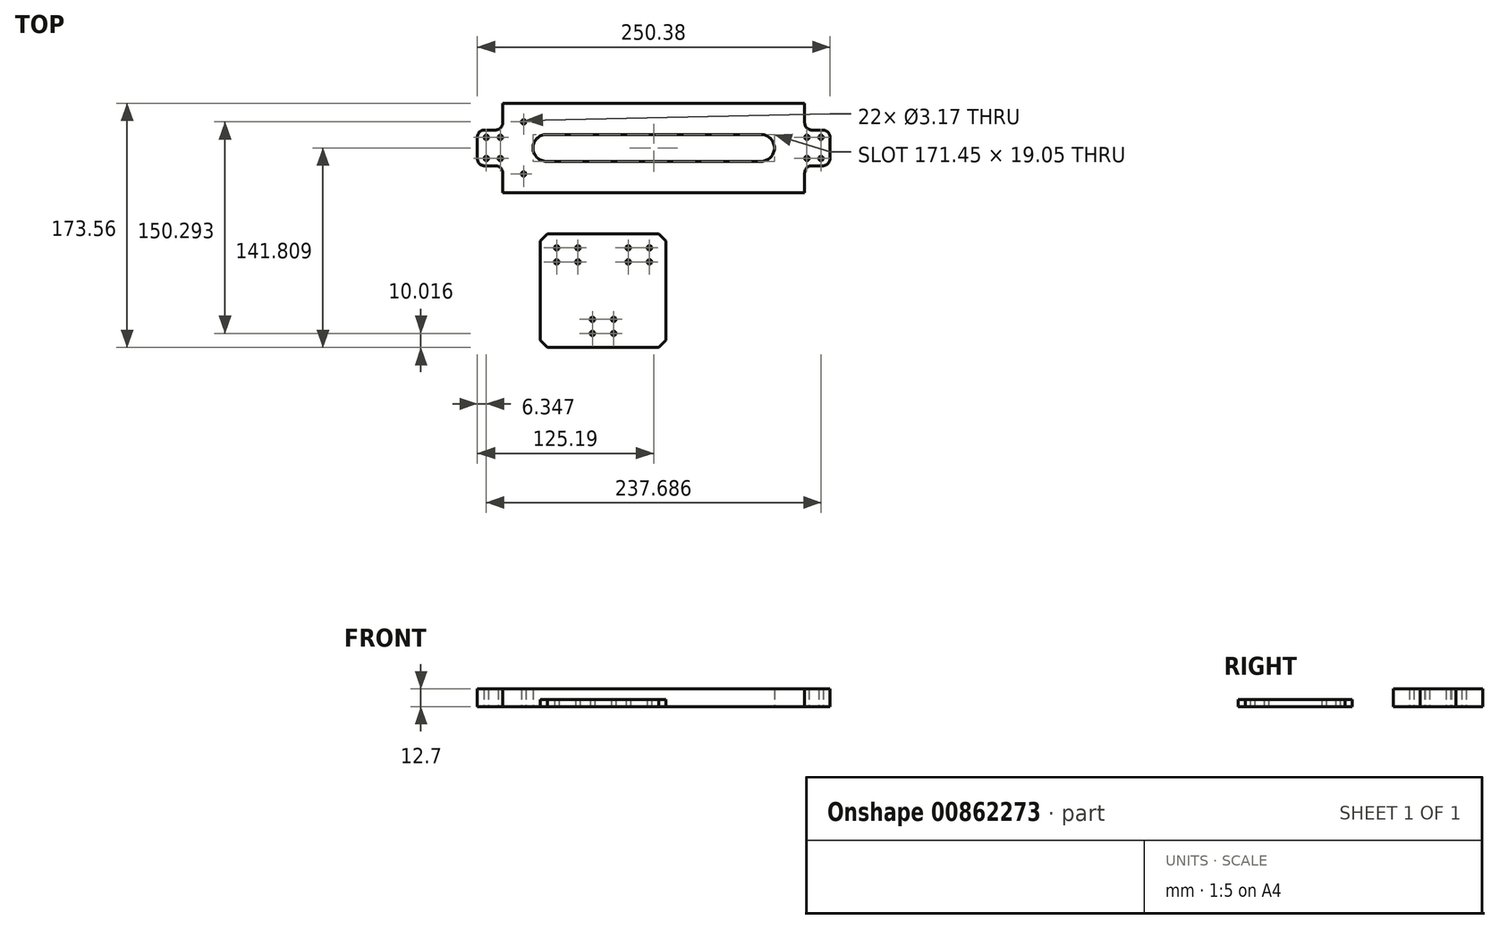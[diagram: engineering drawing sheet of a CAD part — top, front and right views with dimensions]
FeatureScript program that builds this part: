
annotation { "Feature Type Name" : "Feature", "Feature Type Description" : "" }
export const myFeature = defineFeature(function(context is Context, id is Id, definition is map)
    precondition{}
    {
        {
            var Q0;
            Q0=qCreatedBy(makeId("Top.planeOp"),FACE);
            var sketch = newSketch(context, id + "F0", { "sketchPlane" : qUnion([Q0])});
            skLineSegment(sketch, "E0.bottom", {"start": v(-50.02, 48.8) * mm, "end": v(-40.02, 48.8) * mm, "construction": true});
            skLineSegment(sketch, "E0.top", {"start": v(-50.02, 33.8) * mm, "end": v(-40.02, 33.8) * mm, "construction": true});
            skLineSegment(sketch, "E0.left", {"start": v(-50.02, 48.8) * mm, "end": v(-50.02, 33.8) * mm, "construction": true});
            skLineSegment(sketch, "E0.right", {"start": v(-40.02, 48.8) * mm, "end": v(-40.02, 33.8) * mm, "construction": true});
            skPoint(sketch, "E0.middle", {"position": v(-45.02, 41.3) * mm});
            skLineSegment(sketch, "E1.bottom", {"start": v(177.66, 48.8) * mm, "end": v(187.66, 48.8) * mm, "construction": true});
            skLineSegment(sketch, "E1.top", {"start": v(177.66, 33.8) * mm, "end": v(187.66, 33.8) * mm, "construction": true});
            skLineSegment(sketch, "E1.left", {"start": v(177.66, 48.8) * mm, "end": v(177.66, 33.8) * mm, "construction": true});
            skLineSegment(sketch, "E1.right", {"start": v(187.66, 48.8) * mm, "end": v(187.66, 33.8) * mm, "construction": true});
            skPoint(sketch, "E1.middle", {"position": v(182.66, 41.3) * mm});
            skCircle(sketch, "E2", {"center": v(-50.02, 48.8) * mm, "radius": 1.59 * mm});
            skCircle(sketch, "E3", {"center": v(-40.02, 48.8) * mm, "radius": 1.59 * mm});
            skCircle(sketch, "E4", {"center": v(-40.02, 33.8) * mm, "radius": 1.59 * mm});
            skCircle(sketch, "E5", {"center": v(-50.02, 33.8) * mm, "radius": 1.59 * mm});
            skCircle(sketch, "E6", {"center": v(177.66, 33.8) * mm, "radius": 1.59 * mm});
            skCircle(sketch, "E7", {"center": v(187.66, 33.8) * mm, "radius": 1.59 * mm});
            skCircle(sketch, "E8", {"center": v(187.66, 48.8) * mm, "radius": 1.59 * mm});
            skCircle(sketch, "E9", {"center": v(177.66, 48.8) * mm, "radius": 1.59 * mm});
            skLineSegment(sketch, "E10", {"start": v(-45.02, 41.3) * mm, "end": v(182.66, 41.3) * mm, "construction": true});
            skLineSegment(sketch, "E11.bottom", {"start": v(16.5, 66.7) * mm, "end": v(121.14, 66.7) * mm, "construction": true});
            skLineSegment(sketch, "E11.top", {"start": v(16.5, 15.9) * mm, "end": v(121.14, 15.9) * mm, "construction": true});
            skLineSegment(sketch, "E11.left", {"start": v(16.5, 66.7) * mm, "end": v(16.5, 15.9) * mm, "construction": true});
            skLineSegment(sketch, "E11.right", {"start": v(121.14, 66.7) * mm, "end": v(121.14, 15.9) * mm, "construction": true});
            skPoint(sketch, "E11.middle", {"position": v(68.82, 41.3) * mm});
            skLineSegment(sketch, "E12", {"start": v(-56.37, 54) * mm, "end": v(-56.37, 28.6) * mm});
            skLineSegment(sketch, "E13", {"start": v(-56.37, 28.6) * mm, "end": v(-38.44, 28.6) * mm});
            skLineSegment(sketch, "E14", {"start": v(-38.44, 28.6) * mm, "end": v(-38.44, 9.55) * mm});
            skLineSegment(sketch, "E15", {"start": v(-38.44, 9.55) * mm, "end": v(176.08, 9.55) * mm});
            skLineSegment(sketch, "E16", {"start": v(176.08, 9.55) * mm, "end": v(176.08, 28.6) * mm});
            skLineSegment(sketch, "E17", {"start": v(176.08, 28.6) * mm, "end": v(194.01, 28.6) * mm});
            skLineSegment(sketch, "E18", {"start": v(194.01, 28.6) * mm, "end": v(194.01, 54) * mm});
            skLineSegment(sketch, "E19", {"start": v(194.01, 54) * mm, "end": v(176.08, 54) * mm});
            skLineSegment(sketch, "E20", {"start": v(176.08, 54) * mm, "end": v(176.08, 73.05) * mm});
            skLineSegment(sketch, "E21", {"start": v(176.08, 73.05) * mm, "end": v(-38.44, 73.05) * mm});
            skLineSegment(sketch, "E22", {"start": v(-38.44, 73.05) * mm, "end": v(-38.44, 54) * mm});
            skPoint(sketch, "E22.endSnap0", {"position": v(185.04, 54) * mm});
            skLineSegment(sketch, "E23", {"start": v(-38.44, 54) * mm, "end": v(-56.37, 54) * mm});
            skPoint(sketch, "E24", {"position": v(68.82, 73.05) * mm});
            skPoint(sketch, "E25", {"position": v(-56.37, 41.3) * mm});
            skLineSegment(sketch, "E26", {"start": v(-7.38, 41.3) * mm, "end": v(145.02, 41.3) * mm});
            skArc(sketch, "E27.0.startCap", {"start": v(-7.38, 31.77) * mm, "mid": v(-16.9, 41.3) * mm, "end": v(-7.38, 50.82) * mm});
            skArc(sketch, "E27.0.endCap", {"start": v(145.02, 50.82) * mm, "mid": v(154.54, 41.3) * mm, "end": v(145.02, 31.77) * mm});
            skLineSegment(sketch, "E27.0.left", {"start": v(-7.38, 50.82) * mm, "end": v(145.02, 50.82) * mm});
            skLineSegment(sketch, "E27.0.right", {"start": v(-7.38, 31.77) * mm, "end": v(145.02, 31.77) * mm});
            skLineSegment(sketch, "E28", {"start": v(-23.54, 59.8) * mm, "end": v(-23.54, 22.8) * mm, "construction": true});
            skPoint(sketch, "E29", {"position": v(-23.54, 41.3) * mm});
            skCircle(sketch, "E30", {"center": v(-23.54, 59.8) * mm, "radius": 1.59 * mm});
            skCircle(sketch, "E31", {"center": v(-23.54, 22.8) * mm, "radius": 1.59 * mm});
            skSolve(sketch);
        }
        {
            var Q0;
            Q0=makeQuery(id+"F0.imprint","IMPRINT",FACE,{"disambiguationData":[TD([[makeQuery(id+"F0.imprint","IMPRINT",EDGE,{"derivedFrom":sQuery(id+"F0.wireOp",EDGE,"E2")}),-1.0]])]});
            extrude(context, id + "F1", {"entities" : qUnion([Q0]), "depth" : 12.7 * mm, "offsetDistance" : 25.4 * mm});
        }
        {
            var Q0;
            Q0=makeQuery(id+"F1.opExtrude","SWEPT_EDGE",EDGE,{"disambiguationData":[OSD([sQuery(id+"F0.wireOp",EDGE,"E22"),sQuery(id+"F0.wireOp",EDGE,"E23")])]});
            var Q1;
            Q1=makeQuery(id+"F1.opExtrude","SWEPT_EDGE",EDGE,{"disambiguationData":[OSD([sQuery(id+"F0.wireOp",EDGE,"E13"),sQuery(id+"F0.wireOp",EDGE,"E14")])]});
            var Q2;
            Q2=makeQuery(id+"F1.opExtrude","SWEPT_EDGE",EDGE,{"disambiguationData":[OSD([sQuery(id+"F0.wireOp",EDGE,"E16"),sQuery(id+"F0.wireOp",EDGE,"E17")])]});
            var Q3;
            Q3=makeQuery(id+"F1.opExtrude","SWEPT_EDGE",EDGE,{"disambiguationData":[OSD([sQuery(id+"F0.wireOp",EDGE,"E17"),sQuery(id+"F0.wireOp",EDGE,"E18")])]});
            var Q4;
            Q4=makeQuery(id+"F1.opExtrude","SWEPT_EDGE",EDGE,{"disambiguationData":[OSD([sQuery(id+"F0.wireOp",EDGE,"E18"),sQuery(id+"F0.wireOp",EDGE,"E19")])]});
            var Q5;
            Q5=makeQuery(id+"F1.opExtrude","SWEPT_EDGE",EDGE,{"disambiguationData":[OSD([sQuery(id+"F0.wireOp",EDGE,"E19"),sQuery(id+"F0.wireOp",EDGE,"E20")])]});
            var Q6;
            Q6=makeQuery(id+"F1.opExtrude","SWEPT_EDGE",EDGE,{"disambiguationData":[OSD([sQuery(id+"F0.wireOp",EDGE,"E12"),sQuery(id+"F0.wireOp",EDGE,"E13")])]});
            var Q7;
            Q7=makeQuery(id+"F1.opExtrude","SWEPT_EDGE",EDGE,{"disambiguationData":[OSD([sQuery(id+"F0.wireOp",EDGE,"E12"),sQuery(id+"F0.wireOp",EDGE,"E23")])]});
            fillet(context, id + "F2", {"entities" : qUnion([Q0, Q1, Q2, Q3, Q4, Q5, Q6, Q7]), "radius" : 5.08 * mm, "tangentPropagation" : true, "allowEdgeOverflow" : false});
        }
        {
            var Q0;
            Q0=qCreatedBy(makeId("Top.planeOp"),FACE);
            var sketch = newSketch(context, id + "F3", { "sketchPlane" : qUnion([Q0])});
            skLineSegment(sketch, "E32.bottom", {"start": v(-11.55, -19.68) * mm, "end": v(77.35, -19.68) * mm});
            skLineSegment(sketch, "E32.top", {"start": v(-11.55, -100.5) * mm, "end": v(77.35, -100.5) * mm});
            skLineSegment(sketch, "E32.left", {"start": v(-11.55, -19.68) * mm, "end": v(-11.55, -100.5) * mm});
            skLineSegment(sketch, "E32.right", {"start": v(77.35, -19.68) * mm, "end": v(77.35, -100.5) * mm});
            skPoint(sketch, "E32.middle", {"position": v(32.9, -60.1) * mm});
            skLineSegment(sketch, "E33.bottom", {"start": v(25.4, -80.5) * mm, "end": v(40.4, -80.5) * mm, "construction": true});
            skLineSegment(sketch, "E33.top", {"start": v(25.4, -90.5) * mm, "end": v(40.4, -90.5) * mm, "construction": true});
            skLineSegment(sketch, "E33.left", {"start": v(25.4, -80.5) * mm, "end": v(25.4, -90.5) * mm, "construction": true});
            skLineSegment(sketch, "E33.right", {"start": v(40.4, -80.5) * mm, "end": v(40.4, -90.5) * mm, "construction": true});
            skPoint(sketch, "E33.middle", {"position": v(32.9, -85.5) * mm});
            skLineSegment(sketch, "E34", {"start": v(32.9, -60.1) * mm, "end": v(32.9, -19.68) * mm, "construction": true});
            skLineSegment(sketch, "E35.bottom", {"start": v(0, -29.7) * mm, "end": v(15, -29.7) * mm, "construction": true});
            skLineSegment(sketch, "E35.top", {"start": v(0, -39.7) * mm, "end": v(15, -39.7) * mm, "construction": true});
            skLineSegment(sketch, "E35.left", {"start": v(0, -29.7) * mm, "end": v(0, -39.7) * mm, "construction": true});
            skLineSegment(sketch, "E35.right", {"start": v(15, -29.7) * mm, "end": v(15, -39.7) * mm, "construction": true});
            skPoint(sketch, "E35.middle", {"position": v(7.5, -34.7) * mm});
            skCircle(sketch, "E36", {"center": v(0, -29.7) * mm, "radius": 1.59 * mm});
            skCircle(sketch, "E37", {"center": v(0, -39.7) * mm, "radius": 1.59 * mm});
            skCircle(sketch, "E38", {"center": v(15, -39.7) * mm, "radius": 1.59 * mm});
            skCircle(sketch, "E39", {"center": v(15, -29.7) * mm, "radius": 1.59 * mm});
            skLineSegment(sketch, "E40", {"start": v(32.9, -85.5) * mm, "end": v(32.9, -100.5) * mm, "construction": true});
            skLineSegment(sketch, "E41", {"start": v(7.5, -34.7) * mm, "end": v(7.5, -19.68) * mm, "construction": true});
            skCircle(sketch, "E42", {"center": v(25.4, -80.5) * mm, "radius": 1.59 * mm});
            skCircle(sketch, "E43", {"center": v(40.4, -80.5) * mm, "radius": 1.59 * mm});
            skCircle(sketch, "E44", {"center": v(40.4, -90.5) * mm, "radius": 1.59 * mm});
            skCircle(sketch, "E45", {"center": v(25.4, -90.5) * mm, "radius": 1.59 * mm});
            skLineSegment(sketch, "E46.MirrorCS", {"start": v(50.8, -29.7) * mm, "end": v(50.8, -39.7) * mm, "construction": true});
            skLineSegment(sketch, "E47.MirrorCS", {"start": v(65.8, -29.7) * mm, "end": v(50.8, -29.7) * mm, "construction": true});
            skLineSegment(sketch, "E48.MirrorCS", {"start": v(65.8, -39.7) * mm, "end": v(50.8, -39.7) * mm, "construction": true});
            skLineSegment(sketch, "E49.MirrorCS", {"start": v(65.8, -29.7) * mm, "end": v(65.8, -39.7) * mm, "construction": true});
            skCircle(sketch, "E50.MirrorC", {"center": v(50.8, -39.7) * mm, "radius": 1.59 * mm});
            skCircle(sketch, "E51.MirrorC", {"center": v(65.8, -29.7) * mm, "radius": 1.59 * mm});
            skPoint(sketch, "E52.MirrorP", {"position": v(58.3, -34.7) * mm});
            skCircle(sketch, "E53.MirrorC", {"center": v(50.8, -29.7) * mm, "radius": 1.59 * mm});
            skCircle(sketch, "E54.MirrorC", {"center": v(65.8, -39.7) * mm, "radius": 1.59 * mm});
            skSolve(sketch);
        }
        {
            var Q0;
            Q0=makeQuery(id+"F3.imprint","IMPRINT",FACE,{"disambiguationData":[TD([[makeQuery(id+"F3.imprint","IMPRINT",EDGE,{"derivedFrom":sQuery(id+"F3.wireOp",EDGE,"E32.bottom")}),-1.0]])]});
            extrude(context, id + "F4", {"entities" : qUnion([Q0]), "depth" : 5 * mm, "offsetDistance" : 25.4 * mm});
        }
        {
            var Q0;
            Q0=makeQuery(id+"F4.opExtrude","SWEPT_EDGE",EDGE,{"disambiguationData":[OSD([sQuery(id+"F3.wireOp",EDGE,"E32.top"),sQuery(id+"F3.wireOp",EDGE,"E32.left")])]});
            var Q1;
            Q1=makeQuery(id+"F4.opExtrude","SWEPT_EDGE",EDGE,{"disambiguationData":[OSD([sQuery(id+"F3.wireOp",EDGE,"E32.top"),sQuery(id+"F3.wireOp",EDGE,"E32.right")])]});
            var Q2;
            Q2=makeQuery(id+"F4.opExtrude","SWEPT_EDGE",EDGE,{"disambiguationData":[OSD([sQuery(id+"F3.wireOp",EDGE,"E32.bottom"),sQuery(id+"F3.wireOp",EDGE,"E32.left")])]});
            var Q3;
            Q3=makeQuery(id+"F4.opExtrude","SWEPT_EDGE",EDGE,{"disambiguationData":[OSD([sQuery(id+"F3.wireOp",EDGE,"E32.bottom"),sQuery(id+"F3.wireOp",EDGE,"E32.right")])]});
            chamfer(context, id + "F5", {"entities" : qUnion([Q0, Q1, Q2, Q3]), "width" : 5.08 * mm, "tangentPropagation" : true});
        }
    });
